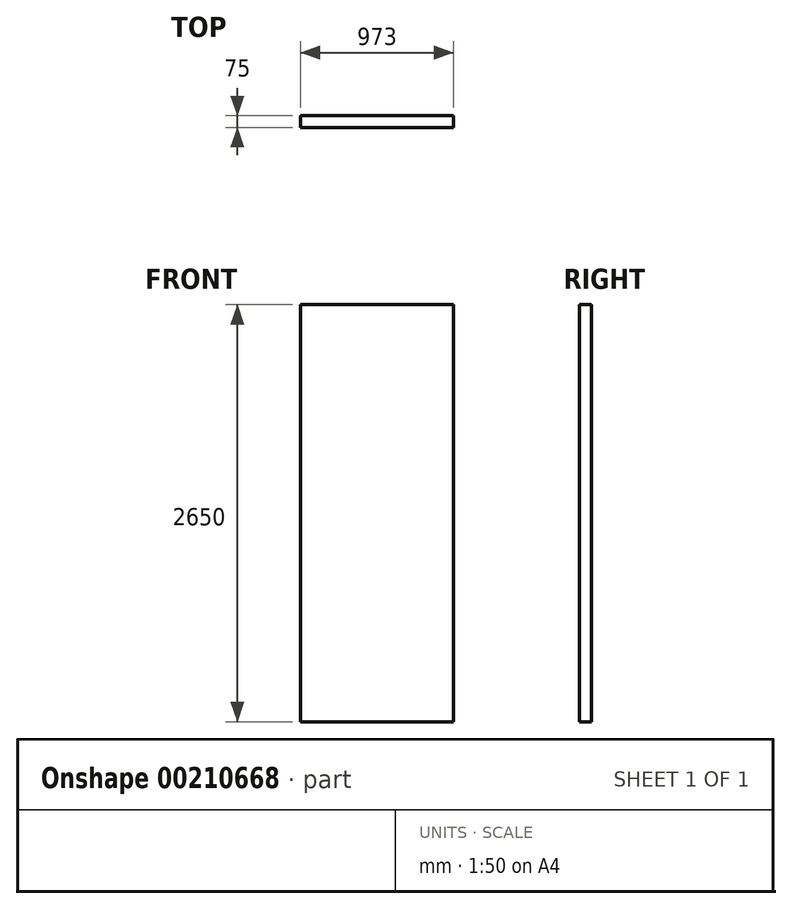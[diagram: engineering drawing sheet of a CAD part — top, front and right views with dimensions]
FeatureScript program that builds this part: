
annotation { "Feature Type Name" : "Feature", "Feature Type Description" : "" }
export const myFeature = defineFeature(function(context is Context, id is Id, definition is map)
    precondition{}
    {
        {
            var Q0;
            Q0=qCreatedBy(makeId("Front.planeOp"),FACE);
            var sketch = newSketch(context, id + "F0", { "sketchPlane" : qUnion([Q0])});
            skLineSegment(sketch, "E0.bottom", {"start": v(0, 0) * mm, "end": v(973, 0) * mm});
            skLineSegment(sketch, "E0.top", {"start": v(0, 2650) * mm, "end": v(973, 2650) * mm});
            skLineSegment(sketch, "E0.left", {"start": v(0, 0) * mm, "end": v(0, 2650) * mm});
            skLineSegment(sketch, "E0.right", {"start": v(973, 0) * mm, "end": v(973, 2650) * mm});
            skSolve(sketch);
        }
        {
            var Q0;
            Q0=makeQuery(id+"F0.imprint","IMPRINT",FACE,{"disambiguationData":[TD([[makeQuery(id+"F0.imprint","IMPRINT",EDGE,{"derivedFrom":sQuery(id+"F0.wireOp",EDGE,"E0.bottom")}),1.0]])]});
            extrude(context, id + "F1", {"entities" : qUnion([Q0]), "depth" : 75 * mm});
        }
    });
